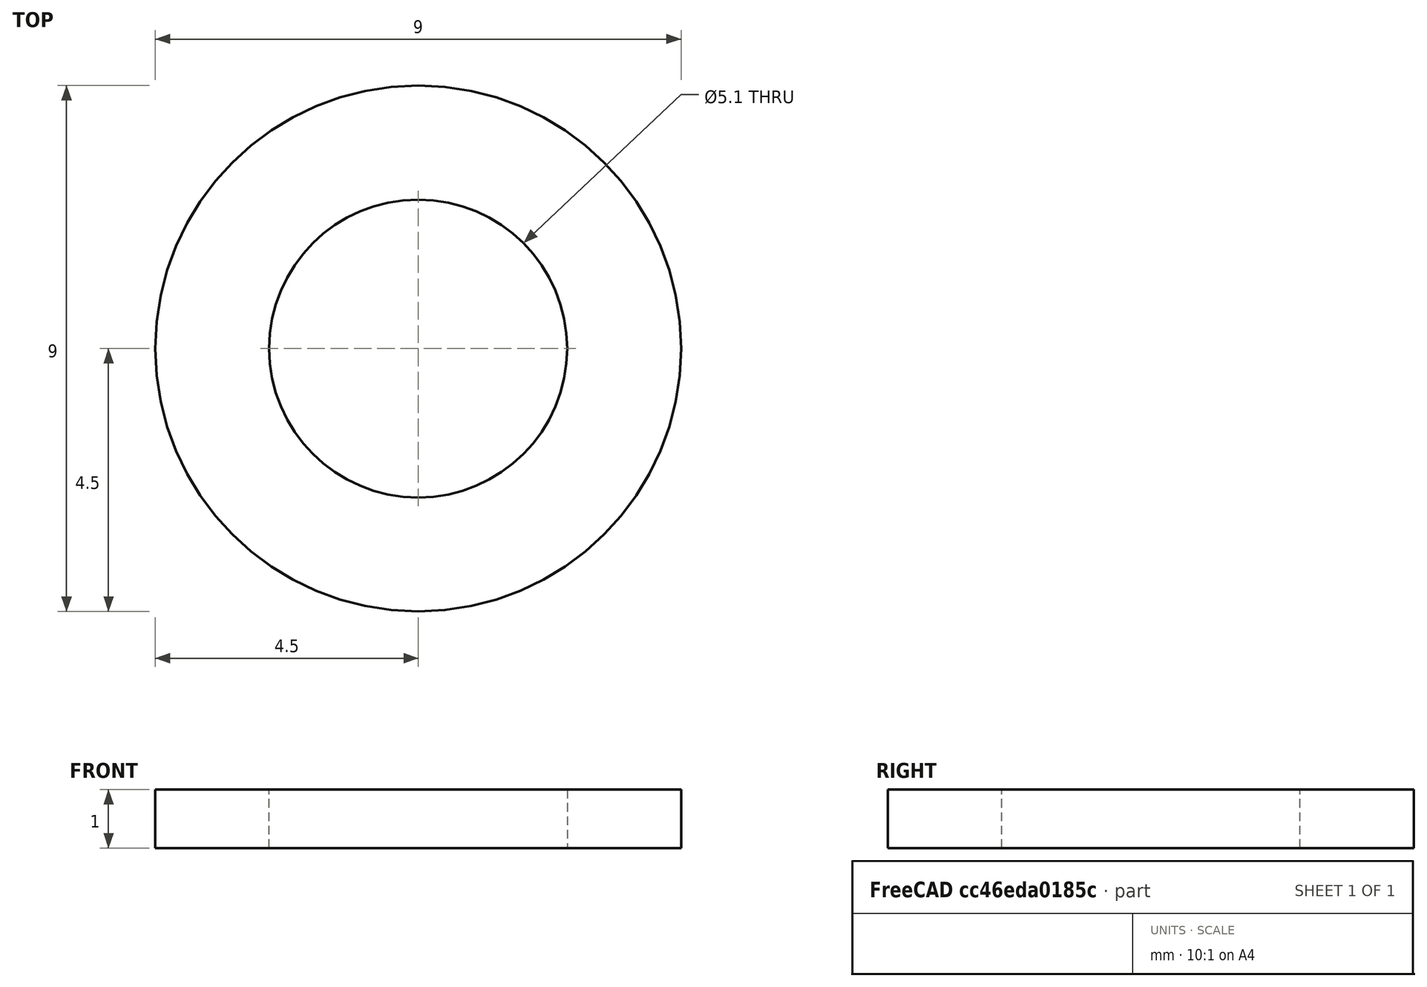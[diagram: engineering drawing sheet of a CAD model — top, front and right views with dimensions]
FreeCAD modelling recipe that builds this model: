
FCSTD DOCUMENT  (FreeCAD 0.17R10495 (Git))
Label: spacer_short
License: All rights reserved
LicenseURL: http://en.wikipedia.org/wiki/All_rights_reserved
objects: Part::Cylinder×1, PartDesign::ShapeBinder×1, Sketcher::SketchObject×1, PartDesign::Pocket×1, PartDesign::Body×1
note: 6 computed .brp shape members not serialized (recipe doc carries the construction recipe); baked Part::Feature solids carry a one-line shape summary decoded from their .brp

FEATURE [Part::Cylinder] Cylinder001
  Angle = 360
  AttacherType = Attacher::AttachEngine3D
  Height = 1
  Placement = pos=(-26,22,0) rot=(0,0,1;0rad)
  Radius = 4.5
FEATURE [PartDesign::ShapeBinder] CopyCylinder001
  Placement = pos=(-26,22,0) rot=(0,0,1;0rad)
FEATURE [Sketcher::SketchObject] Sketch003
  MapMode = 5
  Placement = pos=(-26,22,11) rot=(0,0,1;0rad)
  Support = -> [CopyCylinder001]
  sketch-geometry (1):
    g0: Circle CenterX=0 CenterY=0 CenterZ=0 NormalX=0 NormalY=0 NormalZ=1 Radius=2.55
  constraints (2):
    c: Coincident(g0,g-1)
    c: Radius(g0) = 2.55
FEATURE [PartDesign::Pocket] Pocket002
  BaseFeature = -> Cylinder001
  Length = 5
  Placement = pos=(-26,22,0) rot=(0,0,1;0rad)
  Profile = -> Sketch003
  Type = 1
FEATURE [PartDesign::Body] Body002  label="spacer_short"
  BaseFeature = -> Cylinder001
  Group = -> [CopyCylinder001,Sketch003,Pocket002]
  Origin = -> Body001Origin001
  Tip = -> Pocket002
